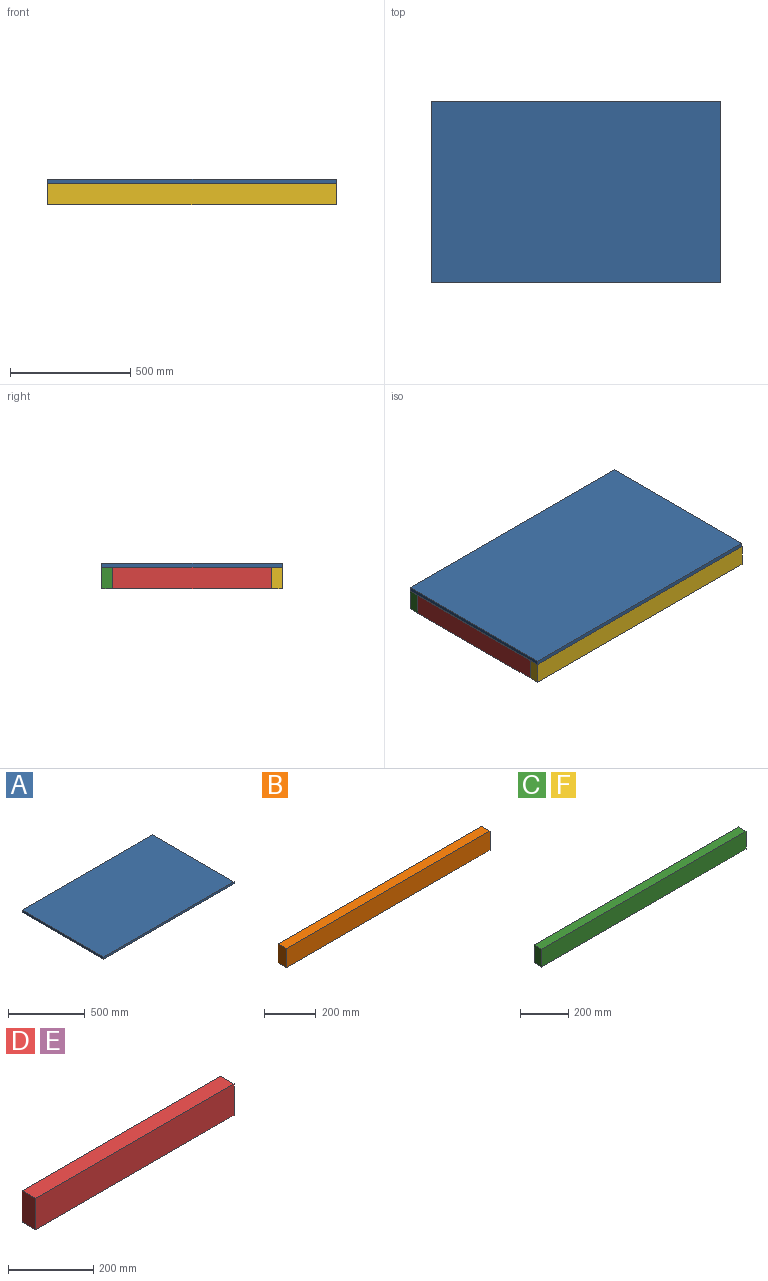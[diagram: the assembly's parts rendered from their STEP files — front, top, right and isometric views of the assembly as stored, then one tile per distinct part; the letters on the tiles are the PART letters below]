
ASSEMBLY  parts=6 mates=5
PART A: 6 faces, bbox 1200x750x17 mm
  f0: plane 1200x750mm, normal (0,0,-1), area 900000mm2, adj f1,f3,f4,f5
  f1: plane 750x17mm, normal (1,0,0), area 12750mm2, adj f0,f2,f4,f5
  f2: plane 1200x750mm, normal (0,0,1), area 900000mm2, adj f1,f3,f4,f5
  f3: plane 750x17mm, normal (-1,0,0), area 12750mm2, adj f0,f2,f4,f5
  f4: plane 1200x17mm, normal (0,-1,0), area 20400mm2, adj f0,f1,f2,f3
  f5: plane 1200x17mm, normal (0,1,0), area 20400mm2, adj f0,f1,f2,f3
PART B: 6 faces, bbox 1110x45x90 mm
  f0: plane 1110x45mm, normal (0,0,1), area 49950mm2, adj f1,f3,f4,f5
  f1: plane 90x45mm, normal (-1,0,0), area 4050mm2, adj f0,f2,f4,f5
  f2: plane 1110x45mm, normal (0,0,-1), area 49950mm2, adj f1,f3,f4,f5
  f3: plane 90x45mm, normal (1,0,0), area 4050mm2, adj f0,f2,f4,f5
  f4: plane 1110x90mm, normal (0,-1,0), area 99900mm2, adj f0,f1,f2,f3
  f5: plane 1110x90mm, normal (0,1,0), area 99900mm2, adj f0,f1,f2,f3
PART C: 6 faces, bbox 1200x45x90 mm
  f0: plane 1200x45mm, normal (0,0,1), area 54000mm2, adj f1,f3,f4,f5
  f1: plane 90x45mm, normal (-1,0,0), area 4050mm2, adj f0,f2,f4,f5
  f2: plane 1200x45mm, normal (0,0,-1), area 54000mm2, adj f1,f3,f4,f5
  f3: plane 90x45mm, normal (1,0,0), area 4050mm2, adj f0,f2,f4,f5
  f4: plane 1200x90mm, normal (0,-1,0), area 108000mm2, adj f0,f1,f2,f3
  f5: plane 1200x90mm, normal (0,1,0), area 108000mm2, adj f0,f1,f2,f3
PART D: 6 faces, bbox 660x45x90 mm
  f0: plane 660x45mm, normal (0,0,1), area 29700mm2, adj f1,f3,f4,f5
  f1: plane 90x45mm, normal (-1,0,0), area 4050mm2, adj f0,f2,f4,f5
  f2: plane 660x45mm, normal (0,0,-1), area 29700mm2, adj f1,f3,f4,f5
  f3: plane 90x45mm, normal (1,0,0), area 4050mm2, adj f0,f2,f4,f5
  f4: plane 660x90mm, normal (0,-1,0), area 59400mm2, adj f0,f1,f2,f3
  f5: plane 660x90mm, normal (0,1,0), area 59400mm2, adj f0,f1,f2,f3
PART E: same geometry as D
PART F: same geometry as C
PLACE A t=(-76.73,258.48,-207.29)mm
PLACE B rot(axis=(0,0,1),180deg) t=(-128.55,235.98,-260.79)mm
PLACE C t=(-128.55,633.48,-260.79)mm
PLACE D rot(axis=(0,0,-1),90deg) t=(-683.55,258.48,-260.79)mm
PLACE E rot(axis=(0,0,-1),90deg) t=(471.45,258.48,-260.79)mm
PLACE F t=(-128.55,-71.52,-260.79)mm
MATE fastened C.f0 <-> A.f0  axis (0,0,-1) through (471.45,633.48,-215.79)mm
MATE fastened A.f0 <-> F.f0  axis (0,0,1) through (-728.55,-116.52,-215.79)mm
MATE fastened D.f2 <-> F.f2  axis (0,0,1) through (-728.55,-71.52,-305.79)mm
MATE fastened E.f5 <-> A.f1  axis (1,0,0) through (471.45,258.48,-215.79)mm
MATE fastened B.f2 <-> D.f2  axis (0,0,-1) through (-683.55,258.48,-305.79)mm
